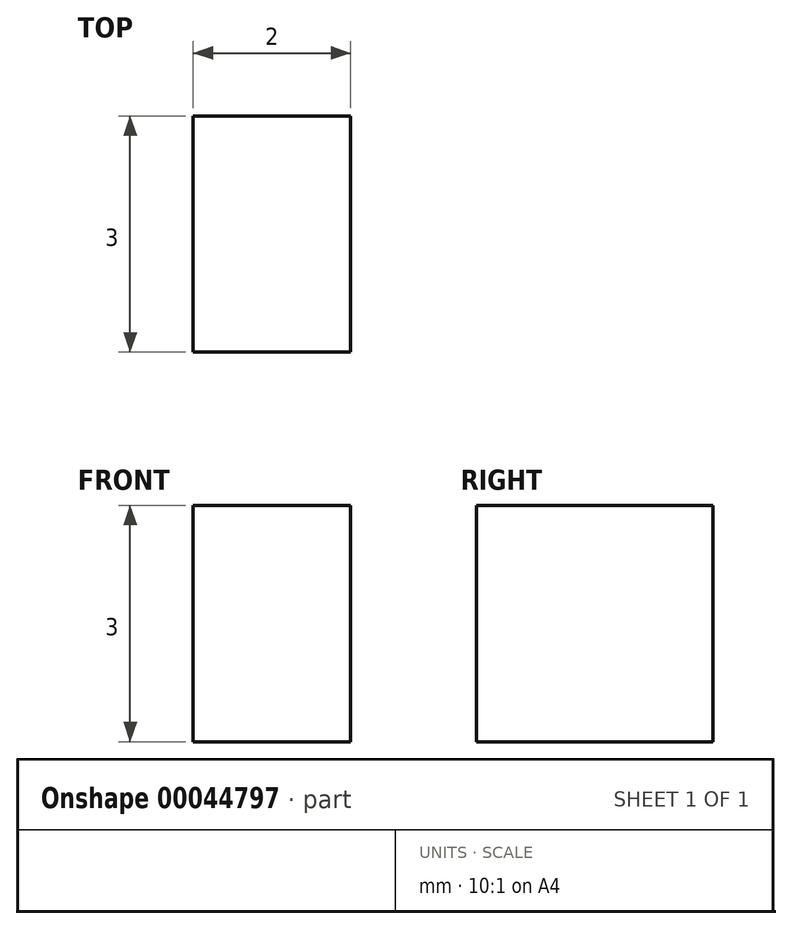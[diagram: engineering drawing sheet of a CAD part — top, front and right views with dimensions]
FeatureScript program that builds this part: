
annotation { "Feature Type Name" : "Feature", "Feature Type Description" : "" }
export const myFeature = defineFeature(function(context is Context, id is Id, definition is map)
    precondition{}
    {
        {
            var Q0;
            Q0=qCreatedBy(makeId("Front.planeOp"),FACE);
            var sketch = newSketch(context, id + "F0", { "sketchPlane" : qUnion([Q0])});
            skLineSegment(sketch, "E0.rect.bottom", {"start": v(4, 42) * mm, "end": v(-4, 42) * mm});
            skLineSegment(sketch, "E0.rect.top", {"start": v(4, -42) * mm, "end": v(-4, -42) * mm});
            skLineSegment(sketch, "E0.rect.left", {"start": v(4, 42) * mm, "end": v(4, -42) * mm});
            skLineSegment(sketch, "E0.rect.right", {"start": v(-4, 42) * mm, "end": v(-4, -42) * mm});
            skPoint(sketch, "E0.rect.middle", {"position": v(0, 0) * mm});
            skCircle(sketch, "E1", {"center": v(-1, 27) * mm, "radius": 1.5 * mm});
            skCircle(sketch, "E2", {"center": v(-1, -33) * mm, "radius": 1.5 * mm});
            skLineSegment(sketch, "E3.bottom", {"start": v(4, 22) * mm, "end": v(2, 22) * mm});
            skLineSegment(sketch, "E3.top", {"start": v(4, 25) * mm, "end": v(2, 25) * mm});
            skLineSegment(sketch, "E3.left", {"start": v(4, 22) * mm, "end": v(4, 25) * mm});
            skLineSegment(sketch, "E3.right", {"start": v(2, 22) * mm, "end": v(2, 25) * mm});
            skLineSegment(sketch, "E4.bottom", {"start": v(4, -31) * mm, "end": v(2, -31) * mm});
            skLineSegment(sketch, "E4.top", {"start": v(4, -28) * mm, "end": v(2, -28) * mm});
            skLineSegment(sketch, "E4.left", {"start": v(4, -31) * mm, "end": v(4, -28) * mm});
            skLineSegment(sketch, "E4.right", {"start": v(2, -31) * mm, "end": v(2, -28) * mm});
            skLineSegment(sketch, "E5.bottom", {"start": v(4, 42) * mm, "end": v(2, 42) * mm});
            skLineSegment(sketch, "E5.top", {"start": v(4, 39) * mm, "end": v(2, 39) * mm});
            skLineSegment(sketch, "E5.left", {"start": v(4, 42) * mm, "end": v(4, 39) * mm});
            skLineSegment(sketch, "E5.right", {"start": v(2, 42) * mm, "end": v(2, 39) * mm});
            skLineSegment(sketch, "E6.bottom", {"start": v(4, -42) * mm, "end": v(2, -42) * mm});
            skLineSegment(sketch, "E6.top", {"start": v(4, -39) * mm, "end": v(2, -39) * mm});
            skLineSegment(sketch, "E6.left", {"start": v(4, -42) * mm, "end": v(4, -39) * mm});
            skLineSegment(sketch, "E6.right", {"start": v(2, -42) * mm, "end": v(2, -39) * mm});
            skLineSegment(sketch, "E7", {"start": v(-1, -42) * mm, "end": v(-1, 42) * mm, "construction": true});
            skSolve(sketch);
        }
        {
            var Q0;
            Q0=makeQuery(id+"F0.imprint","IMPRINT",FACE,{"disambiguationData":[TD([[makeQuery(id+"F0.imprint","IMPRINT",EDGE,{"derivedFrom":sQuery(id+"F0.wireOp",EDGE,"E0.rect.bottom")}),1.0]])]});
            extrude(context, id + "F1", {"entities" : qUnion([Q0]), "depth" : 3 * mm});
        }
    });
